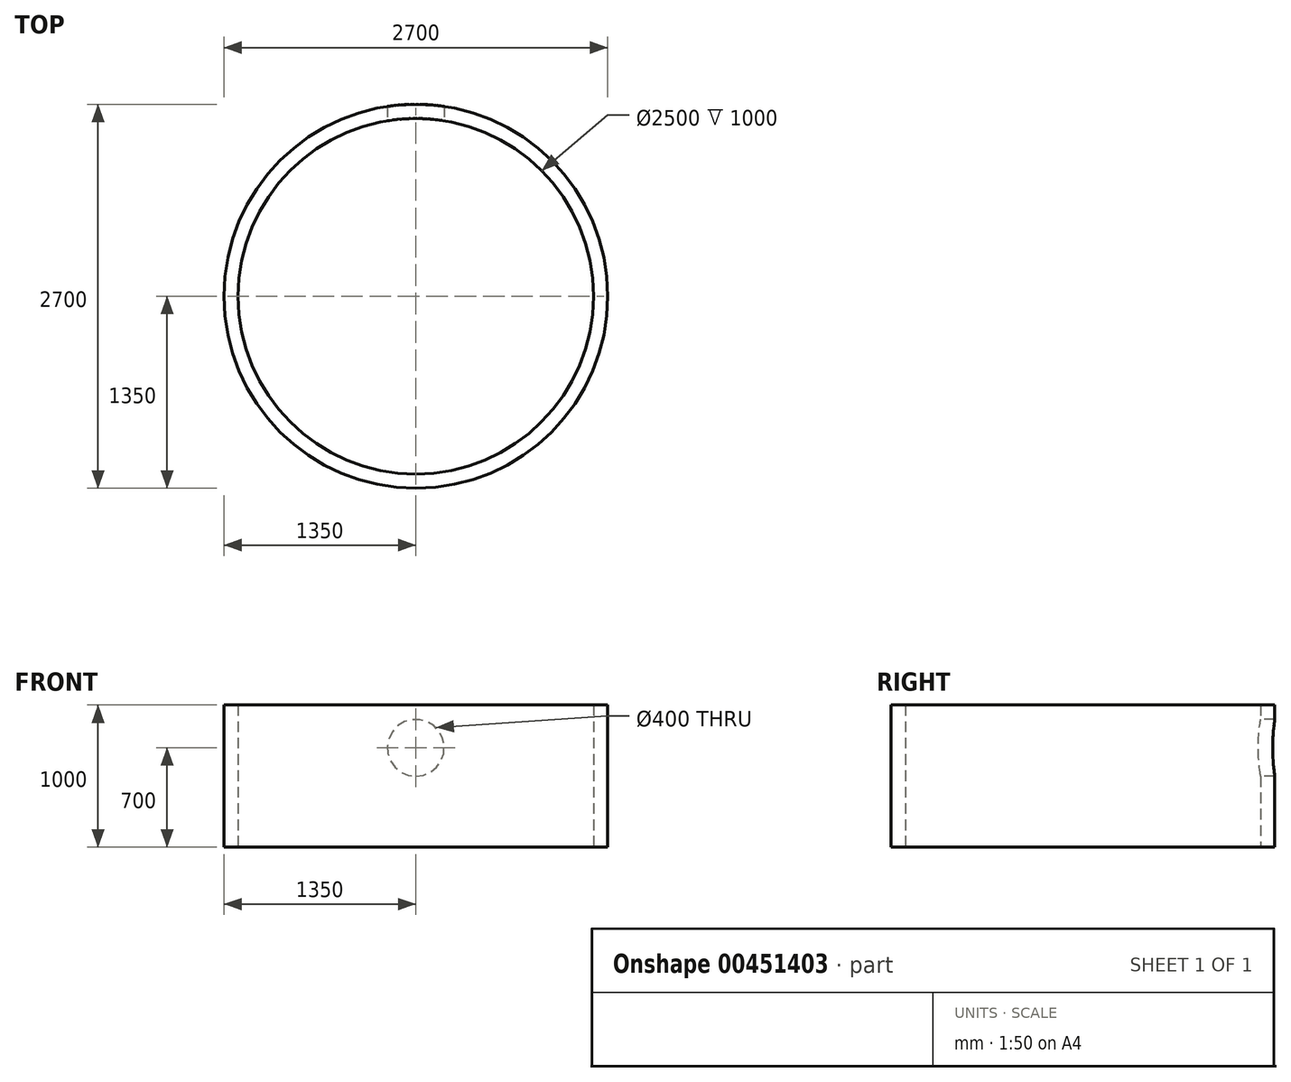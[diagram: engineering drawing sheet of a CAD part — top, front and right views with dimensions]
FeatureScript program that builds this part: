
annotation { "Feature Type Name" : "Feature", "Feature Type Description" : "" }
export const myFeature = defineFeature(function(context is Context, id is Id, definition is map)
    precondition{}
    {
        {
            var Q0;
            Q0=qCreatedBy(makeId("Top.planeOp"),FACE);
            var sketch = newSketch(context, id + "F0", { "sketchPlane" : qUnion([Q0])});
            skCircle(sketch, "E0", {"center": v(0, 0) * mm, "radius": 1250 * mm});
            skCircle(sketch, "E1", {"center": v(0, 0) * mm, "radius": 1350 * mm});
            skSolve(sketch);
        }
        {
            var Q0;
            Q0 = qSketchRegion(id + "F0", true);
            extrude(context, id + "F1", {"entities" : qUnion([Q0]), "endBound" : BoundingType.SYMMETRIC, "depth" : 1000 * mm, "offsetDistance" : 25 * mm});
        }
        {
            var Q0;
            Q0=qCreatedBy(makeId("Front.planeOp"),FACE);
            var sketch = newSketch(context, id + "F2", { "sketchPlane" : qUnion([Q0])});
            skCircle(sketch, "E2", {"center": v(0, 200) * mm, "radius": 200 * mm});
            skSolve(sketch);
        }
        {
            var Q0;
            Q0=makeQuery(id+"F2.imprint","IMPRINT",FACE,{"disambiguationData":[TD([[makeQuery(id+"F2.imprint","IMPRINT",EDGE,{"derivedFrom":sQuery(id+"F2.wireOp",EDGE,"E2")}),1.0]])]});
            extrude(context, id + "F3", {"entities" : qUnion([Q0]), "operationType" : NewBodyOperationType.REMOVE, "oppositeDirection" : true, "depth" : 2000 * mm, "offsetDistance" : 25 * mm});
        }
    });
